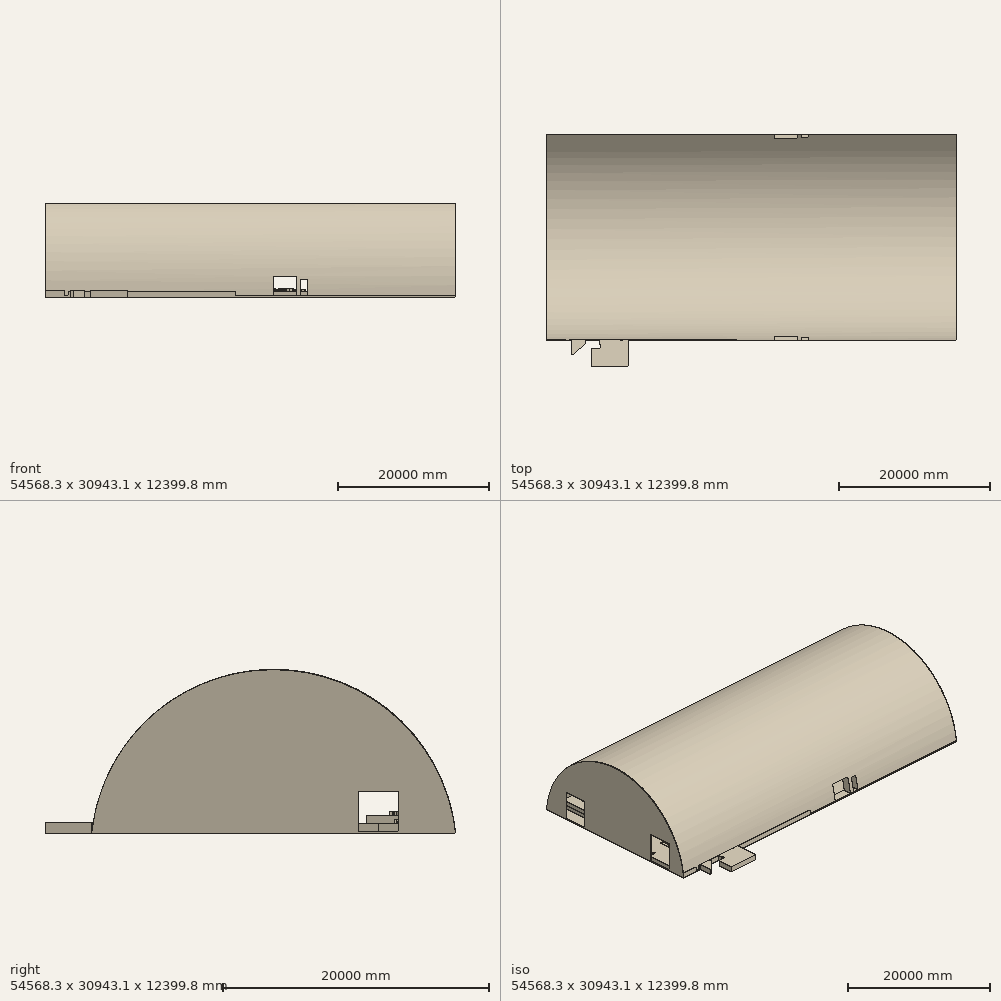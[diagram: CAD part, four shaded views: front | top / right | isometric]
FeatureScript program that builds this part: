
annotation { "Feature Type Name" : "Feature", "Feature Type Description" : "" }
export const myFeature = defineFeature(function(context is Context, id is Id, definition is map)
    precondition{}
    {
        {
            var Q0;
            Q0=qCreatedBy(makeId("Top.planeOp"),FACE);
            var sketch = newSketch(context, id + "F0", { "sketchPlane" : qUnion([Q0])});
            skLineSegment(sketch, "E0.bottom", {"start": v(0, 0) * mm, "end": v(54507.38, 0) * mm});
            skLineSegment(sketch, "E0.top", {"start": v(0, 27432) * mm, "end": v(54507.38, 27432) * mm});
            skLineSegment(sketch, "E0.left", {"start": v(0, 0) * mm, "end": v(0, 27432) * mm});
            skLineSegment(sketch, "E0.right", {"start": v(54507.38, 0) * mm, "end": v(54507.38, 27432) * mm});
            skSolve(sketch);
        }
        {
            var Q0;
            Q0 = qSketchRegion(id + "F0", true);
            extrude(context, id + "F1", {"entities" : qUnion([Q0]), "depth" : 152.4 * mm});
        }
        {
            var Q0;
            Q0=qCreatedBy(makeId("Right.planeOp"),FACE);
            var sketch = newSketch(context, id + "F2", { "sketchPlane" : qUnion([Q0])});
            skArc(sketch, "E1", {"start": v(27437.9, 83.16) * mm, "mid": v(13750, 12399.77) * mm, "end": v(0, 152.55) * mm});
            skArc(sketch, "E2.0", {"start": v(26210.86, 83.16) * mm, "mid": v(13750.05, 11180.56) * mm, "end": v(1227.79, 152.55) * mm});
            skLineSegment(sketch, "E3", {"start": v(0, 152.55) * mm, "end": v(1227.79, 152.55) * mm});
            skLineSegment(sketch, "E4", {"start": v(27437.9, 83.16) * mm, "end": v(26210.86, 83.16) * mm});
            skSolve(sketch);
        }
        {
            var Q0;
            Q0 = qSketchRegion(id + "F2", true);
            extrude(context, id + "F3", {"entities" : qUnion([Q0]), "depth" : 54507.38 * mm});
        }
        {
            var Q0;
            Q0=makeQuery(id+"F1.opExtrude","SWEPT_FACE",FACE,{"disambiguationData":[OSD([sQuery(id+"F0.wireOp",EDGE,"E0.right")])]});
            var sketch = newSketch(context, id + "F4", { "sketchPlane" : qUnion([Q0])});
            skArc(sketch, "E5", {"start": v(27432, 152.4) * mm, "mid": v(13716, 12374) * mm, "end": v(0, 152.4) * mm});
            skLineSegment(sketch, "E6", {"start": v(0, 152.4) * mm, "end": v(0, 0) * mm});
            skLineSegment(sketch, "E7", {"start": v(0, 0) * mm, "end": v(27432, 0) * mm});
            skLineSegment(sketch, "E8", {"start": v(27432, 0) * mm, "end": v(27432, 152.4) * mm});
            skSolve(sketch);
        }
        {
            var Q0;
            Q0 = qSketchRegion(id + "F4", true);
            extrude(context, id + "F5", {"entities" : qUnion([Q0]), "depth" : 30.48 * mm});
        }
        {
            var Q0;
            Q0=makeQuery(id+"F1.opExtrude","SWEPT_FACE",FACE,{"disambiguationData":[OSD([sQuery(id+"F0.wireOp",EDGE,"E0.left")])]});
            var sketch = newSketch(context, id + "F6", { "sketchPlane" : qUnion([Q0])});
            skArc(sketch, "E9", {"start": v(0, 152.4) * mm, "mid": v(-13716, 12352.94) * mm, "end": v(-27432, 152.4) * mm});
            skLineSegment(sketch, "E10", {"start": v(-27432, 152.4) * mm, "end": v(-27432, 0) * mm});
            skLineSegment(sketch, "E11", {"start": v(-27432, 0) * mm, "end": v(0, 0) * mm});
            skLineSegment(sketch, "E12", {"start": v(0, 0) * mm, "end": v(0, 152.4) * mm});
            skSolve(sketch);
        }
        {
            var Q0;
            Q0 = qSketchRegion(id + "F6", true);
            extrude(context, id + "F7", {"entities" : qUnion([Q0]), "depth" : 30.48 * mm});
        }
        {
            var Q0;
            Q0=makeQuery(id+"F7.opExtrude","CAP_FACE",FACE,{"disambiguationData":[OSD([sQuery(id+"F6.wireOp",EDGE,"E9"),sQuery(id+"F6.wireOp",EDGE,"E10"),sQuery(id+"F6.wireOp",EDGE,"E11"),sQuery(id+"F6.wireOp",EDGE,"E12")])],"isStart":false});
            var sketch = newSketch(context, id + "F8", { "sketchPlane" : qUnion([Q0])});
            skLineSegment(sketch, "E13.bottom", {"start": v(-2895.6, 152.4) * mm, "end": v(-6553.2, 152.4) * mm});
            skLineSegment(sketch, "E13.top", {"start": v(-2895.6, 4419.6) * mm, "end": v(-6553.2, 4419.6) * mm});
            skLineSegment(sketch, "E13.left", {"start": v(-2895.6, 152.4) * mm, "end": v(-2895.6, 4419.6) * mm});
            skLineSegment(sketch, "E13.right", {"start": v(-6553.2, 152.4) * mm, "end": v(-6553.2, 4419.6) * mm});
            skLineSegment(sketch, "E14.bottom", {"start": v(-23469.6, 4419.6) * mm, "end": v(-19812, 4419.6) * mm});
            skLineSegment(sketch, "E14.top", {"start": v(-23469.6, 152.4) * mm, "end": v(-19812, 152.4) * mm});
            skLineSegment(sketch, "E14.left", {"start": v(-23469.6, 4419.6) * mm, "end": v(-23469.6, 152.4) * mm});
            skLineSegment(sketch, "E14.right", {"start": v(-19812, 4419.6) * mm, "end": v(-19812, 152.4) * mm});
            skSolve(sketch);
        }
        {
            var Q0;
            Q0 = qSketchRegion(id + "F8", true);
            extrude(context, id + "F9", {"entities" : qUnion([Q0]), "operationType" : NewBodyOperationType.REMOVE, "endBound" : BoundingType.UP_TO_NEXT, "oppositeDirection" : true, "depth" : 30.48 * mm});
        }
        {
            var Q0;
            Q0=makeQuery(id+"F5.opExtrude","CAP_FACE",FACE,{"disambiguationData":[OSD([sQuery(id+"F4.wireOp",EDGE,"E5"),sQuery(id+"F4.wireOp",EDGE,"E6"),sQuery(id+"F4.wireOp",EDGE,"E7"),sQuery(id+"F4.wireOp",EDGE,"E8")])],"isStart":false});
            var sketch = newSketch(context, id + "F10", { "sketchPlane" : qUnion([Q0])});
            skLineSegment(sketch, "E15.bottom", {"start": v(23164.8, 152.4) * mm, "end": v(20116.8, 152.4) * mm});
            skLineSegment(sketch, "E15.top", {"start": v(23164.8, 3200.4) * mm, "end": v(20116.8, 3200.4) * mm});
            skLineSegment(sketch, "E15.left", {"start": v(23164.8, 152.4) * mm, "end": v(23164.8, 3200.4) * mm});
            skLineSegment(sketch, "E15.right", {"start": v(20116.8, 152.4) * mm, "end": v(20116.8, 3200.4) * mm});
            skSolve(sketch);
        }
        {
            var Q0;
            Q0 = qSketchRegion(id + "F10", true);
            extrude(context, id + "F11", {"entities" : qUnion([Q0]), "operationType" : NewBodyOperationType.REMOVE, "endBound" : BoundingType.UP_TO_NEXT, "oppositeDirection" : true, "depth" : 30.48 * mm});
        }
        {
            var Q0;
            Q0=qCreatedBy(makeId("Front.planeOp"),FACE);
            var sketch = newSketch(context, id + "F12", { "sketchPlane" : qUnion([Q0])});
            skLineSegment(sketch, "E16.bottom", {"start": v(33323.78, 2673.96) * mm, "end": v(30275.78, 2673.96) * mm});
            skLineSegment(sketch, "E16.top", {"start": v(33323.78, 235.56) * mm, "end": v(30275.78, 235.56) * mm});
            skLineSegment(sketch, "E16.left", {"start": v(33323.78, 2673.96) * mm, "end": v(33323.78, 235.56) * mm});
            skLineSegment(sketch, "E16.right", {"start": v(30275.78, 2673.96) * mm, "end": v(30275.78, 235.56) * mm});
            skLineSegment(sketch, "E17.bottom", {"start": v(34796.98, 2369.16) * mm, "end": v(33933.38, 2369.16) * mm});
            skLineSegment(sketch, "E17.top", {"start": v(34796.98, 235.56) * mm, "end": v(33933.38, 235.56) * mm});
            skLineSegment(sketch, "E17.left", {"start": v(34796.98, 2369.16) * mm, "end": v(34796.98, 235.56) * mm});
            skLineSegment(sketch, "E17.right", {"start": v(33933.38, 2369.16) * mm, "end": v(33933.38, 235.56) * mm});
            skSolve(sketch);
        }
        {
            var Q0;
            Q0 = qSketchRegion(id + "F12", true);
            extrude(context, id + "F13", {"entities" : qUnion([Q0]), "operationType" : NewBodyOperationType.REMOVE, "endBound" : BoundingType.THROUGH_ALL, "oppositeDirection" : true, "depth" : 30.48 * mm});
        }
        {
            var Q0;
            Q0=qCreatedBy(makeId("Top.planeOp"),FACE);
            var sketch = newSketch(context, id + "F14", { "sketchPlane" : qUnion([Q0])});
            skLineSegment(sketch, "E18", {"start": v(0, 0) * mm, "end": v(0, 2438.4) * mm});
            skLineSegment(sketch, "E19", {"start": v(0, 2438.4) * mm, "end": v(9753.6, 2438.4) * mm});
            skLineSegment(sketch, "E20", {"start": v(0, 0) * mm, "end": v(2438.4, 0) * mm});
            skLineSegment(sketch, "E21", {"start": v(2438.4, 0) * mm, "end": v(2438.4, 609.6) * mm});
            skLineSegment(sketch, "E22", {"start": v(2438.4, 609.6) * mm, "end": v(3352.8, 609.6) * mm});
            skLineSegment(sketch, "E23", {"start": v(3352.8, 609.6) * mm, "end": v(3352.8, -1905) * mm});
            skLineSegment(sketch, "E24", {"start": v(3352.8, -1905) * mm, "end": v(3657.6, -1905) * mm});
            skLineSegment(sketch, "E25", {"start": v(9753.6, 2438.4) * mm, "end": v(9753.6, 0) * mm});
            skLineSegment(sketch, "E26", {"start": v(9753.6, 0) * mm, "end": v(10261.7, 0) * mm});
            skLineSegment(sketch, "E27", {"start": v(10261.7, 0) * mm, "end": v(10261.7, 152.4) * mm});
            skLineSegment(sketch, "E28", {"start": v(10261.7, 152.4) * mm, "end": v(10871.3, 152.4) * mm});
            skLineSegment(sketch, "E29", {"start": v(10871.3, 152.4) * mm, "end": v(10871.3, -3505.2) * mm});
            skLineSegment(sketch, "E30", {"start": v(10871.3, -3505.2) * mm, "end": v(5994.5, -3505.2) * mm});
            skLineSegment(sketch, "E31", {"start": v(5994.5, -3505.2) * mm, "end": v(5994.5, -1066.8) * mm});
            skLineSegment(sketch, "E32", {"start": v(5994.5, -1066.8) * mm, "end": v(7152.74, -1066.8) * mm});
            skLineSegment(sketch, "E33", {"start": v(7152.74, -1066.8) * mm, "end": v(7152.74, -558.7) * mm});
            skLineSegment(sketch, "E34", {"start": v(7152.74, -558.7) * mm, "end": v(7000.34, -558.7) * mm});
            skLineSegment(sketch, "E35", {"start": v(7000.34, -558.7) * mm, "end": v(7000.34, 965.3) * mm});
            skLineSegment(sketch, "E36", {"start": v(7000.34, 965.3) * mm, "end": v(6492.24, 965.3) * mm});
            skLineSegment(sketch, "E37", {"start": v(6492.24, 965.3) * mm, "end": v(6492.24, 812.9) * mm});
            skLineSegment(sketch, "E38", {"start": v(6492.24, 812.9) * mm, "end": v(5171.54, 812.9) * mm});
            skLineSegment(sketch, "E39", {"start": v(5171.54, 812.9) * mm, "end": v(5171.54, -406.3) * mm});
            skLineSegment(sketch, "E40", {"start": v(5171.54, -406.3) * mm, "end": v(3657.6, -1905) * mm});
            skSolve(sketch);
        }
        {
            var Q0;
            Q0 = qSketchRegion(id + "F14", true);
            extrude(context, id + "F15", {"entities" : qUnion([Q0]), "depth" : 812.8 * mm});
        }
        {
            var Q0;
            Q0=qCreatedBy(makeId("Top.planeOp"),FACE);
            var sketch = newSketch(context, id + "F16", { "sketchPlane" : qUnion([Q0])});
            skLineSegment(sketch, "E41", {"start": v(0, 0) * mm, "end": v(0, 6705.6) * mm});
            skLineSegment(sketch, "E42", {"start": v(0, 0) * mm, "end": v(1295.4, 0) * mm});
            skLineSegment(sketch, "E43", {"start": v(1295.4, 0) * mm, "end": v(1295.4, 505.97) * mm});
            skLineSegment(sketch, "E44", {"start": v(1295.4, 505.97) * mm, "end": v(2819.4, 505.97) * mm});
            skLineSegment(sketch, "E45", {"start": v(2819.4, 505.97) * mm, "end": v(2819.4, 4163.57) * mm});
            skLineSegment(sketch, "E46", {"start": v(2819.4, 4163.57) * mm, "end": v(2514.6, 4163.57) * mm});
            skLineSegment(sketch, "E47", {"start": v(2514.6, 4163.57) * mm, "end": v(2514.6, 4669.54) * mm});
            skLineSegment(sketch, "E48", {"start": v(2514.6, 4669.54) * mm, "end": v(3657.6, 4669.54) * mm});
            skLineSegment(sketch, "E49", {"start": v(3657.6, 4669.54) * mm, "end": v(3657.6, 8327.14) * mm});
            skLineSegment(sketch, "E50", {"start": v(0, 6705.6) * mm, "end": v(1219.2, 6705.6) * mm});
            skLineSegment(sketch, "E51", {"start": v(1219.2, 6705.6) * mm, "end": v(1219.2, 7211.57) * mm});
            skLineSegment(sketch, "E52", {"start": v(1219.2, 7211.57) * mm, "end": v(914.4, 7211.57) * mm});
            skLineSegment(sketch, "E53", {"start": v(914.4, 7211.57) * mm, "end": v(914.4, 8202.06) * mm});
            skLineSegment(sketch, "E54", {"start": v(3657.6, 8327.14) * mm, "end": v(4876.8, 8327.14) * mm});
            skLineSegment(sketch, "E55", {"start": v(4876.8, 8327.14) * mm, "end": v(4876.8, 10765.54) * mm});
            skLineSegment(sketch, "E56", {"start": v(4876.8, 10765.54) * mm, "end": v(3175, 10765.54) * mm});
            skLineSegment(sketch, "E57", {"start": v(914.4, 8202.06) * mm, "end": v(914.4, 10765.54) * mm});
            skLineSegment(sketch, "E58", {"start": v(914.4, 10765.54) * mm, "end": v(609.6, 10765.54) * mm});
            skLineSegment(sketch, "E59", {"start": v(609.6, 10765.54) * mm, "end": v(609.6, 14727.94) * mm});
            skLineSegment(sketch, "E60", {"start": v(609.6, 14727.94) * mm, "end": v(4572, 14727.94) * mm});
            skLineSegment(sketch, "E61", {"start": v(4572, 14727.94) * mm, "end": v(4572, 13508.74) * mm});
            skLineSegment(sketch, "E62", {"start": v(4572, 13508.74) * mm, "end": v(2807.5, 13508.74) * mm});
            skLineSegment(sketch, "E63", {"start": v(2807.5, 13508.74) * mm, "end": v(2807.5, 13051.54) * mm});
            skLineSegment(sketch, "E64", {"start": v(2807.5, 13051.54) * mm, "end": v(3175, 13051.54) * mm});
            skLineSegment(sketch, "E65", {"start": v(3175, 13051.54) * mm, "end": v(3175, 10765.54) * mm});
            skSolve(sketch);
        }
        {
            var Q0;
            Q0 = qSketchRegion(id + "F16", true);
            extrude(context, id + "F17", {"entities" : qUnion([Q0]), "depth" : 812.8 * mm});
        }
        {
            var Q0;
            Q0=makeQuery(id+"F1.opExtrude","CAP_FACE",FACE,{"disambiguationData":[OSD([sQuery(id+"F0.wireOp",EDGE,"E0.bottom"),sQuery(id+"F0.wireOp",EDGE,"E0.top"),sQuery(id+"F0.wireOp",EDGE,"E0.left"),sQuery(id+"F0.wireOp",EDGE,"E0.right")])],"isStart":false});
            var sketch = newSketch(context, id + "F18", { "sketchPlane" : qUnion([Q0])});
            skLineSegment(sketch, "E66.bottom", {"start": v(3048, 0) * mm, "end": v(25298.4, 0) * mm});
            skLineSegment(sketch, "E66.top", {"start": v(3048, 4267.2) * mm, "end": v(25298.4, 4267.2) * mm});
            skLineSegment(sketch, "E66.left", {"start": v(3048, 0) * mm, "end": v(3048, 4267.2) * mm});
            skLineSegment(sketch, "E66.right", {"start": v(25298.4, 0) * mm, "end": v(25298.4, 4267.2) * mm});
            skSolve(sketch);
        }
        {
            var Q0;
            Q0 = qSketchRegion(id + "F18", true);
            extrude(context, id + "F19", {"entities" : qUnion([Q0]), "operationType" : NewBodyOperationType.ADD, "depth" : 609.6 * mm});
        }
        {
            var Q0;
            Q0=makeQuery(id+"F1.opExtrude","CAP_FACE",FACE,{"disambiguationData":[OSD([sQuery(id+"F0.wireOp",EDGE,"E0.bottom"),sQuery(id+"F0.wireOp",EDGE,"E0.top"),sQuery(id+"F0.wireOp",EDGE,"E0.left"),sQuery(id+"F0.wireOp",EDGE,"E0.right")])],"isStart":false});
            var sketch = newSketch(context, id + "F20", { "sketchPlane" : qUnion([Q0])});
            skLineSegment(sketch, "E67.bottom", {"start": v(49935.38, 26212.8) * mm, "end": v(40791.38, 26212.8) * mm});
            skLineSegment(sketch, "E67.top", {"start": v(49935.38, 21640.8) * mm, "end": v(40791.38, 21640.8) * mm});
            skLineSegment(sketch, "E67.left", {"start": v(49935.38, 26212.8) * mm, "end": v(49935.38, 21640.8) * mm});
            skLineSegment(sketch, "E67.right", {"start": v(40791.38, 26212.8) * mm, "end": v(40791.38, 21640.8) * mm});
            skSolve(sketch);
        }
        {
            var Q0;
            Q0 = qSketchRegion(id + "F20", true);
            extrude(context, id + "F21", {"entities" : qUnion([Q0]), "operationType" : NewBodyOperationType.ADD, "depth" : 609.6 * mm});
        }
        {
            var Q0;
            Q0=makeQuery(id+"F21.opExtrude","CAP_FACE",FACE,{"disambiguationData":[OSD([sQuery(id+"F20.wireOp",EDGE,"E67.bottom"),sQuery(id+"F20.wireOp",EDGE,"E67.top"),sQuery(id+"F20.wireOp",EDGE,"E67.left"),sQuery(id+"F20.wireOp",EDGE,"E67.right")])],"isStart":false});
            var sketch = newSketch(context, id + "F22", { "sketchPlane" : qUnion([Q0])});
            skText(sketch, "E68", { "text": "Paint area\n", "fontName": "OpenSans-Regular.ttf"});
            skText(sketch, "E69", { "text": "Storage racks (finished goods)", "fontName": "OpenSans-Regular.ttf"});
            const initialGuessF22  = {"E68": [41.64375, 23.02455, 1, 0, 1.13293], "E69": [4.3765, 1.44943, 1, 0, 0.92361]};
            skSetInitialGuess(sketch, initialGuessF22);
            skSolve(sketch);
        }
        {
            var Q0;
            Q0 = qSketchRegion(id + "F22", true);
            extrude(context, id + "F23", {"entities" : qUnion([Q0]), "operationType" : NewBodyOperationType.ADD, "depth" : 152.4 * mm});
        }
        {
            var Q0;
            Q0=makeQuery(id+"F1.opExtrude","CAP_FACE",FACE,{"disambiguationData":[OSD([sQuery(id+"F0.wireOp",EDGE,"E0.bottom"),sQuery(id+"F0.wireOp",EDGE,"E0.top"),sQuery(id+"F0.wireOp",EDGE,"E0.left"),sQuery(id+"F0.wireOp",EDGE,"E0.right")])],"isStart":false});
            extrude(context, id + "F24", {"entities" : qUnion([Q0]), "depth" : 30.48 * mm});
        }
        {
            var Q0;
            Q0=makeQuery(id+"F24.opExtrude","CAP_FACE",FACE,{"disambiguationData":[OSD([sQuery(id+"F0.wireOp",EDGE,"E0.bottom"),sQuery(id+"F0.wireOp",EDGE,"E0.top"),sQuery(id+"F0.wireOp",EDGE,"E0.left"),sQuery(id+"F0.wireOp",EDGE,"E0.right")])],"isStart":false});
            var sketch = newSketch(context, id + "F25", { "sketchPlane" : qUnion([Q0])});
            skLineSegment(sketch, "E70.bottom", {"start": v(304.8, 19812) * mm, "end": v(2743.2, 19812) * mm});
            skLineSegment(sketch, "E70.top", {"start": v(304.8, 7620) * mm, "end": v(2743.2, 7620) * mm});
            skLineSegment(sketch, "E70.right", {"start": v(2743.2, 19812) * mm, "end": v(2743.2, 7620) * mm});
            skLineSegment(sketch, "E71", {"start": v(304.8, 19812) * mm, "end": v(304.8, 7620) * mm});
            skSolve(sketch);
        }
        {
            var Q0;
            Q0 = qSketchRegion(id + "F25", true);
            extrude(context, id + "F26", {"entities" : qUnion([Q0]), "operationType" : NewBodyOperationType.ADD, "depth" : 609.6 * mm});
        }
        {
            var Q0;
            Q0=makeQuery(id+"F26.opExtrude","CAP_FACE",FACE,{"disambiguationData":[OSD([sQuery(id+"F25.wireOp",EDGE,"E70.bottom"),sQuery(id+"F25.wireOp",EDGE,"E70.top"),sQuery(id+"F25.wireOp",EDGE,"E70.right"),sQuery(id+"F25.wireOp",EDGE,"E71")])],"isStart":false});
            var sketch = newSketch(context, id + "F27", { "sketchPlane" : qUnion([Q0])});
            skLineSegment(sketch, "E72.bottom", {"start": v(1828.8, 26822.4) * mm, "end": v(20116.8, 26822.4) * mm});
            skLineSegment(sketch, "E72.top", {"start": v(1828.8, 20726.4) * mm, "end": v(20116.8, 20726.4) * mm});
            skLineSegment(sketch, "E72.left", {"start": v(1828.8, 26822.4) * mm, "end": v(1828.8, 20726.4) * mm});
            skLineSegment(sketch, "E72.right", {"start": v(20116.8, 26822.4) * mm, "end": v(20116.8, 20726.4) * mm});
            skSolve(sketch);
        }
        {
            var Q0;
            Q0 = qSketchRegion(id + "F27", true);
            extrude(context, id + "F28", {"entities" : qUnion([Q0]), "depth" : 609.6 * mm});
        }
        {
            var Q0;
            Q0=makeQuery(id+"F28.opExtrude","CAP_FACE",FACE,{"disambiguationData":[OSD([sQuery(id+"F27.wireOp",EDGE,"E72.bottom"),sQuery(id+"F27.wireOp",EDGE,"E72.top"),sQuery(id+"F27.wireOp",EDGE,"E72.left"),sQuery(id+"F27.wireOp",EDGE,"E72.right")])],"isStart":false});
            var sketch = newSketch(context, id + "F29", { "sketchPlane" : qUnion([Q0])});
            skText(sketch, "E73", { "text": "Boat fitting/ SRT installs", "fontName": "OpenSans-Regular.ttf"});
            const initialGuessF29  = {"E73": [3.46678, 22.765, 1, 0, 1.03437]};
            skSetInitialGuess(sketch, initialGuessF29);
            skSolve(sketch);
        }
        {
            var Q0;
            Q0 = qSketchRegion(id + "F29", true);
            extrude(context, id + "F30", {"entities" : qUnion([Q0]), "operationType" : NewBodyOperationType.ADD, "depth" : 304.8 * mm});
        }
        {
            var Q0;
            Q0=makeQuery(id+"F24.opExtrude","CAP_FACE",FACE,{"disambiguationData":[OSD([sQuery(id+"F0.wireOp",EDGE,"E0.bottom"),sQuery(id+"F0.wireOp",EDGE,"E0.top"),sQuery(id+"F0.wireOp",EDGE,"E0.left"),sQuery(id+"F0.wireOp",EDGE,"E0.right")])],"isStart":false});
            var sketch = newSketch(context, id + "F31", { "sketchPlane" : qUnion([Q0])});
            skLineSegment(sketch, "E74.bottom", {"start": v(24027.38, 26212.8) * mm, "end": v(36219.38, 26212.8) * mm});
            skLineSegment(sketch, "E74.top", {"start": v(24027.38, 20116.8) * mm, "end": v(36219.38, 20116.8) * mm});
            skLineSegment(sketch, "E74.left", {"start": v(24027.38, 26212.8) * mm, "end": v(24027.38, 20116.8) * mm});
            skLineSegment(sketch, "E74.right", {"start": v(36219.38, 26212.8) * mm, "end": v(36219.38, 20116.8) * mm});
            skSolve(sketch);
        }
        {
            var Q0;
            Q0 = qSketchRegion(id + "F31", true);
            extrude(context, id + "F32", {"entities" : qUnion([Q0]), "operationType" : NewBodyOperationType.ADD, "depth" : 609.6 * mm});
        }
        {
            var Q0;
            Q0=makeQuery(id+"F32.opExtrude","CAP_FACE",FACE,{"disambiguationData":[OSD([sQuery(id+"F31.wireOp",EDGE,"E74.bottom"),sQuery(id+"F31.wireOp",EDGE,"E74.top"),sQuery(id+"F31.wireOp",EDGE,"E74.left"),sQuery(id+"F31.wireOp",EDGE,"E74.right")])],"isStart":false});
            var sketch = newSketch(context, id + "F33", { "sketchPlane" : qUnion([Q0])});
            skText(sketch, "E75", { "text": "Welding", "fontName": "OpenSans-Regular.ttf"});
            const initialGuessF33  = {"E75": [25.6828, 23.32444, 1, 0, 1.3995]};
            skSetInitialGuess(sketch, initialGuessF33);
            skSolve(sketch);
        }
        {
            var Q0;
            Q0 = qSketchRegion(id + "F33", true);
            extrude(context, id + "F34", {"entities" : qUnion([Q0]), "operationType" : NewBodyOperationType.ADD, "depth" : 304.8 * mm});
        }
        {
            var Q0;
            Q0=makeQuery(id+"F1.opExtrude","CAP_FACE",FACE,{"disambiguationData":[OSD([sQuery(id+"F0.wireOp",EDGE,"E0.bottom"),sQuery(id+"F0.wireOp",EDGE,"E0.top"),sQuery(id+"F0.wireOp",EDGE,"E0.left"),sQuery(id+"F0.wireOp",EDGE,"E0.right")])],"isStart":false});
            var sketch = newSketch(context, id + "F35", { "sketchPlane" : qUnion([Q0])});
            skLineSegment(sketch, "E76.bottom", {"start": v(36219.38, 26212.8) * mm, "end": v(27075.38, 26212.8) * mm});
            skLineSegment(sketch, "E76.top", {"start": v(36219.38, 21640.8) * mm, "end": v(27075.38, 21640.8) * mm});
            skLineSegment(sketch, "E76.left", {"start": v(36219.38, 26212.8) * mm, "end": v(36219.38, 21640.8) * mm});
            skLineSegment(sketch, "E76.right", {"start": v(27075.38, 26212.8) * mm, "end": v(27075.38, 21640.8) * mm});
            skLineSegment(sketch, "E77.bottom", {"start": v(1828.8, 26212.8) * mm, "end": v(20116.8, 26212.8) * mm});
            skLineSegment(sketch, "E77.top", {"start": v(1828.8, 20116.8) * mm, "end": v(20116.8, 20116.8) * mm});
            skLineSegment(sketch, "E77.left", {"start": v(1828.8, 26212.8) * mm, "end": v(1828.8, 20116.8) * mm});
            skLineSegment(sketch, "E77.right", {"start": v(20116.8, 26212.8) * mm, "end": v(20116.8, 20116.8) * mm});
            skLineSegment(sketch, "E78.bottom", {"start": v(1219.2, 19507.2) * mm, "end": v(4267.2, 19507.2) * mm});
            skLineSegment(sketch, "E78.top", {"start": v(1219.2, 7315.2) * mm, "end": v(4267.2, 7315.2) * mm});
            skLineSegment(sketch, "E78.left", {"start": v(1219.2, 19507.2) * mm, "end": v(1219.2, 7315.2) * mm});
            skLineSegment(sketch, "E78.right", {"start": v(4267.2, 19507.2) * mm, "end": v(4267.2, 7315.2) * mm});
            skSolve(sketch);
        }
        {
            var Q0;
            Q0 = qSketchRegion(id + "F35", true);
            extrude(context, id + "F36", {"entities" : qUnion([Q0]), "operationType" : NewBodyOperationType.ADD, "depth" : 609.6 * mm});
        }
        {
            var Q0;
            Q0=makeQuery(id+"F36.opExtrude","CAP_FACE",FACE,{"disambiguationData":[OSD([sQuery(id+"F35.wireOp",EDGE,"E77.bottom"),sQuery(id+"F35.wireOp",EDGE,"E77.top"),sQuery(id+"F35.wireOp",EDGE,"E77.left"),sQuery(id+"F35.wireOp",EDGE,"E77.right")])],"isStart":false});
            var sketch = newSketch(context, id + "F37", { "sketchPlane" : qUnion([Q0])});
            skText(sketch, "E79", { "text": "Boat fitting /\nSide roll install\n", "fontName": "OpenSans-Regular.ttf"});
            skPoint(sketch, "E79.secondSnap0", {"position": v(1828.8, 23164.8) * mm});
            skText(sketch, "E80", { "text": "Welding", "fontName": "OpenSans-Regular.ttf"});
            const initialGuessF37  = {"E79": [2.7936, 23.1648, 1, 0, 0.96579], "E80": [28.78875, 23.52835, 1, 0, 1.1076]};
            skSetInitialGuess(sketch, initialGuessF37);
            skSolve(sketch);
        }
        {
            var Q0;
            Q0 = qSketchRegion(id + "F37", true);
            extrude(context, id + "F38", {"entities" : qUnion([Q0]), "operationType" : NewBodyOperationType.ADD, "depth" : 304.8 * mm});
        }
    });
